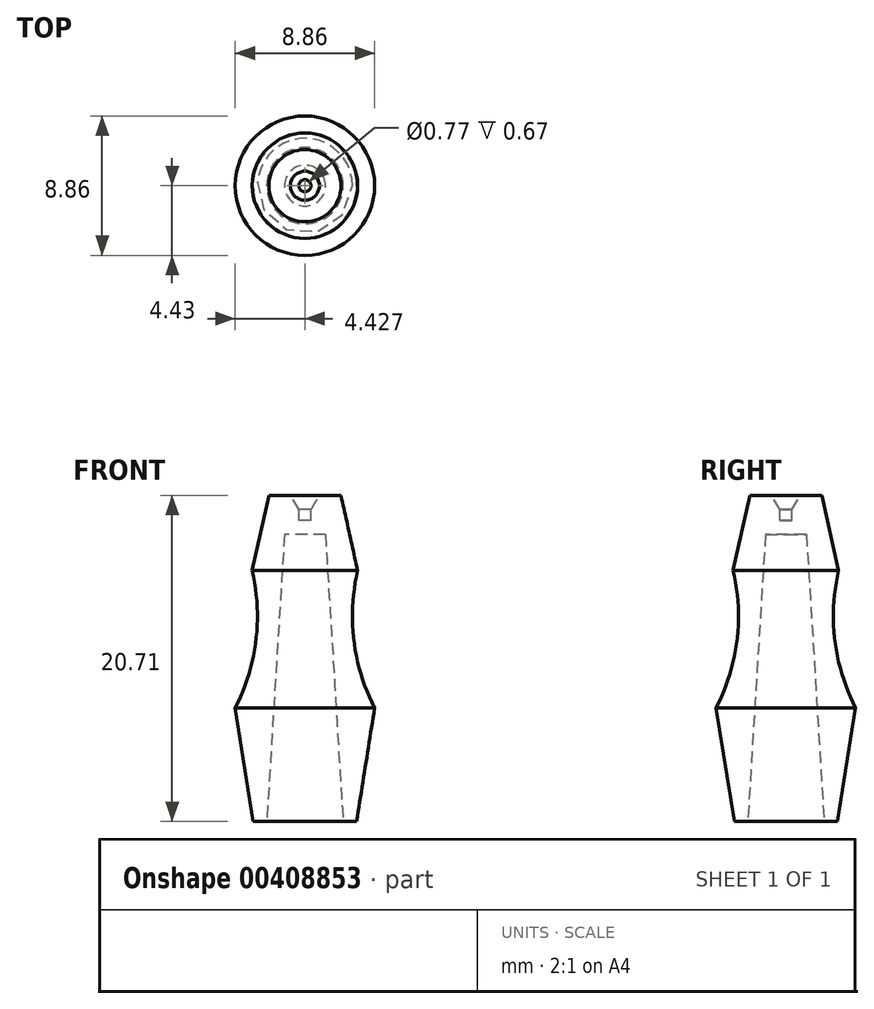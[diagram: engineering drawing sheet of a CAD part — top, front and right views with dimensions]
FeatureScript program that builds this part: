
annotation { "Feature Type Name" : "Feature", "Feature Type Description" : "" }
export const myFeature = defineFeature(function(context is Context, id is Id, definition is map)
    precondition{}
    {
        {
            var Q0;
            Q0=qCreatedBy(makeId("Front.planeOp"),FACE);
            var sketch = newSketch(context, id + "F0", { "sketchPlane" : qUnion([Q0])});
            skLineSegment(sketch, "E0", {"start": v(-5.74, 10.14) * mm, "end": v(-5.74, -10.33) * mm, "construction": true});
            skLineSegment(sketch, "E1", {"start": v(-4.83, 10.54) * mm, "end": v(-3.45, 10.54) * mm});
            skLineSegment(sketch, "E2", {"start": v(-3.45, 10.54) * mm, "end": v(-2.4, 5.77) * mm});
            skArc(sketch, "E3", {"start": v(-2.4, 5.77) * mm, "mid": v(-2.63, 1.32) * mm, "end": v(-1.31, -2.94) * mm});
            skLineSegment(sketch, "E4", {"start": v(-1.31, -2.94) * mm, "end": v(-2.46, -10.17) * mm});
            skLineSegment(sketch, "E5", {"start": v(-2.46, -10.17) * mm, "end": v(-3.32, -10.17) * mm});
            skLineSegment(sketch, "E6", {"start": v(-3.32, -10.17) * mm, "end": v(-4.44, 8.07) * mm});
            skLineSegment(sketch, "E7", {"start": v(-4.44, 8.07) * mm, "end": v(-5.74, 8.07) * mm});
            skLineSegment(sketch, "E8", {"start": v(-5.74, 8.07) * mm, "end": v(-5.74, 8.97) * mm});
            skLineSegment(sketch, "E9", {"start": v(-5.74, 8.97) * mm, "end": v(-5.36, 8.97) * mm});
            skLineSegment(sketch, "E10", {"start": v(-5.36, 8.97) * mm, "end": v(-5.36, 9.64) * mm});
            skLineSegment(sketch, "E11", {"start": v(-5.36, 9.64) * mm, "end": v(-4.83, 10.54) * mm});
            skSolve(sketch);
        }
        {
            var Q0;
            Q0 = qSketchRegion(id + "F0", true);
            var Q1;
            Q1=sQuery(id+"F0.wireOp",EDGE,"E0");
            revolve(context, id + "F1", {"entities" : qUnion([Q0]), "axis" : qUnion([Q1]), "revolveType" : RevolveType.FULL});
        }
    });
